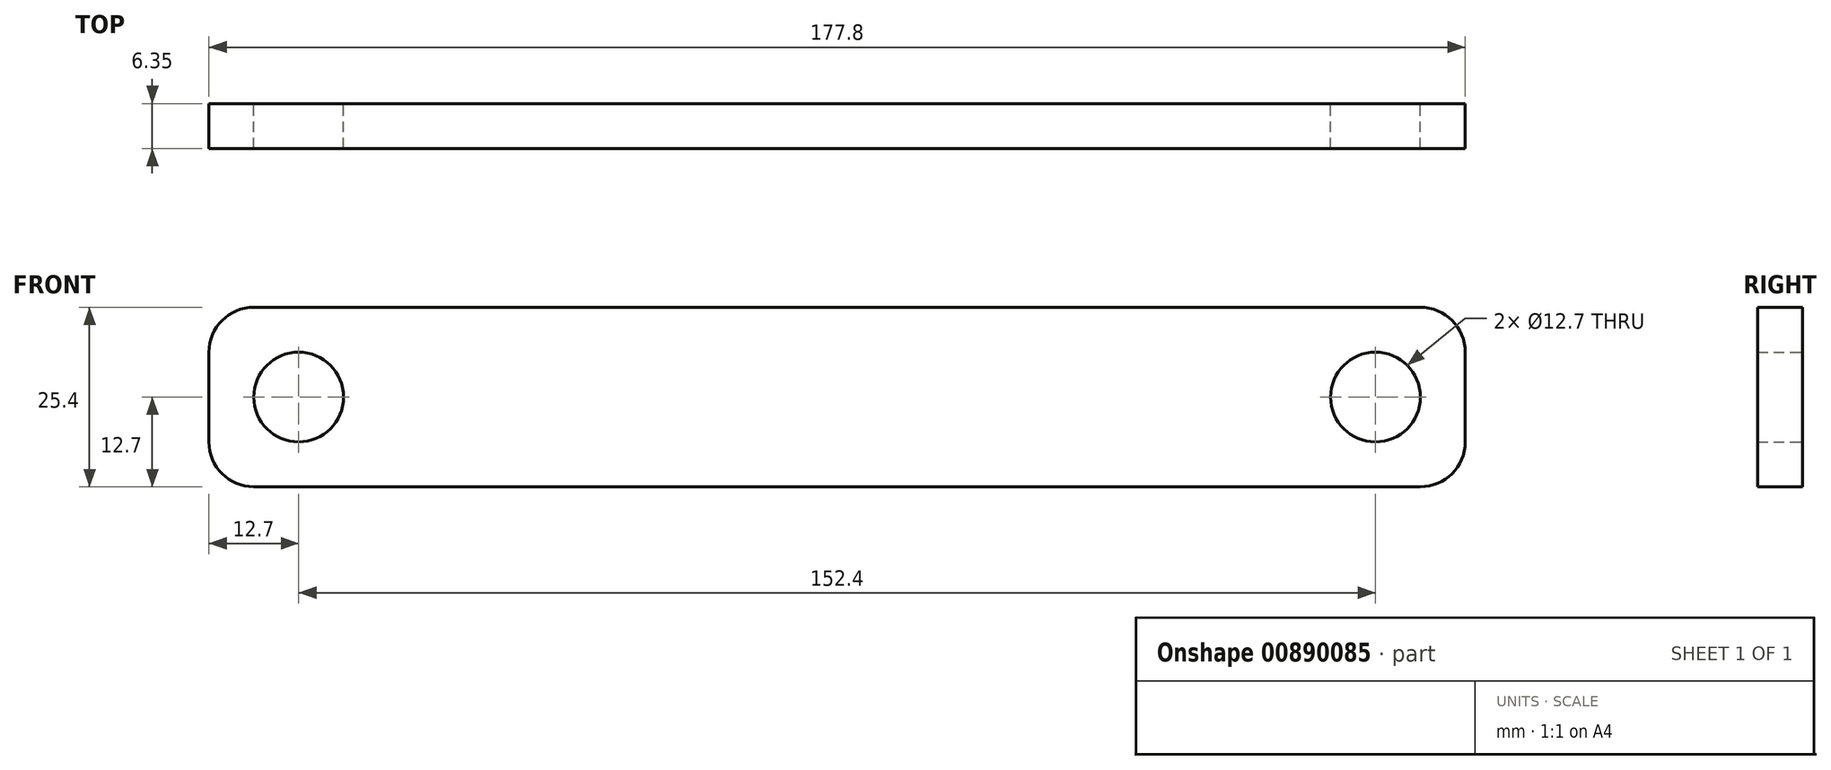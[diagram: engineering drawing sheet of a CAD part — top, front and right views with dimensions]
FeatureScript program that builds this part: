
annotation { "Feature Type Name" : "Feature", "Feature Type Description" : "" }
export const myFeature = defineFeature(function(context is Context, id is Id, definition is map)
    precondition{}
    {
        {
            var Q0;
            Q0=qCreatedBy(makeId("Front.planeOp"),FACE);
            var sketch = newSketch(context, id + "F0", { "sketchPlane" : qUnion([Q0])});
            skLineSegment(sketch, "E0.bottom", {"start": v(-6.35, 12.7) * mm, "end": v(158.75, 12.7) * mm});
            skLineSegment(sketch, "E0.top", {"start": v(-6.35, -12.7) * mm, "end": v(158.75, -12.7) * mm});
            skLineSegment(sketch, "E0.left", {"start": v(-12.7, 6.35) * mm, "end": v(-12.7, -6.35) * mm});
            skLineSegment(sketch, "E0.right", {"start": v(165.1, 6.35) * mm, "end": v(165.1, -6.35) * mm});
            skLineSegment(sketch, "E1", {"start": v(-12.7, 0) * mm, "end": v(165.1, 0) * mm, "construction": true});
            skCircle(sketch, "E2", {"center": v(0, 0) * mm, "radius": 6.35 * mm});
            skCircle(sketch, "E3", {"center": v(152.4, 0) * mm, "radius": 6.35 * mm});
            skLineSegment(sketch, "E4", {"start": v(76.2, 12.7) * mm, "end": v(76.2, -12.7) * mm, "construction": true});
            skPoint(sketch, "E5.visualSharp", {"position": v(-12.7, 12.7) * mm});
            skArc(sketch, "E5.filletArc", {"start": v(-6.35, 12.7) * mm, "mid": v(-10.84, 10.84) * mm, "end": v(-12.7, 6.35) * mm});
            skPoint(sketch, "E6.visualSharp", {"position": v(-12.7, -12.7) * mm});
            skArc(sketch, "E6.filletArc", {"start": v(-12.7, -6.35) * mm, "mid": v(-10.84, -10.84) * mm, "end": v(-6.35, -12.7) * mm});
            skPoint(sketch, "E7.visualSharp", {"position": v(165.1, 12.7) * mm});
            skArc(sketch, "E7.filletArc", {"start": v(165.1, 6.35) * mm, "mid": v(163.24, 10.84) * mm, "end": v(158.75, 12.7) * mm});
            skPoint(sketch, "E8.visualSharp", {"position": v(165.1, -12.7) * mm});
            skArc(sketch, "E8.filletArc", {"start": v(158.75, -12.7) * mm, "mid": v(163.24, -10.84) * mm, "end": v(165.1, -6.35) * mm});
            skSolve(sketch);
        }
        {
            var Q0;
            Q0 = qSketchRegion(id + "F0", true);
            extrude(context, id + "F1", {"entities" : qUnion([Q0]), "depth" : 6.35 * mm, "offsetDistance" : 25.4 * mm});
        }
    });
